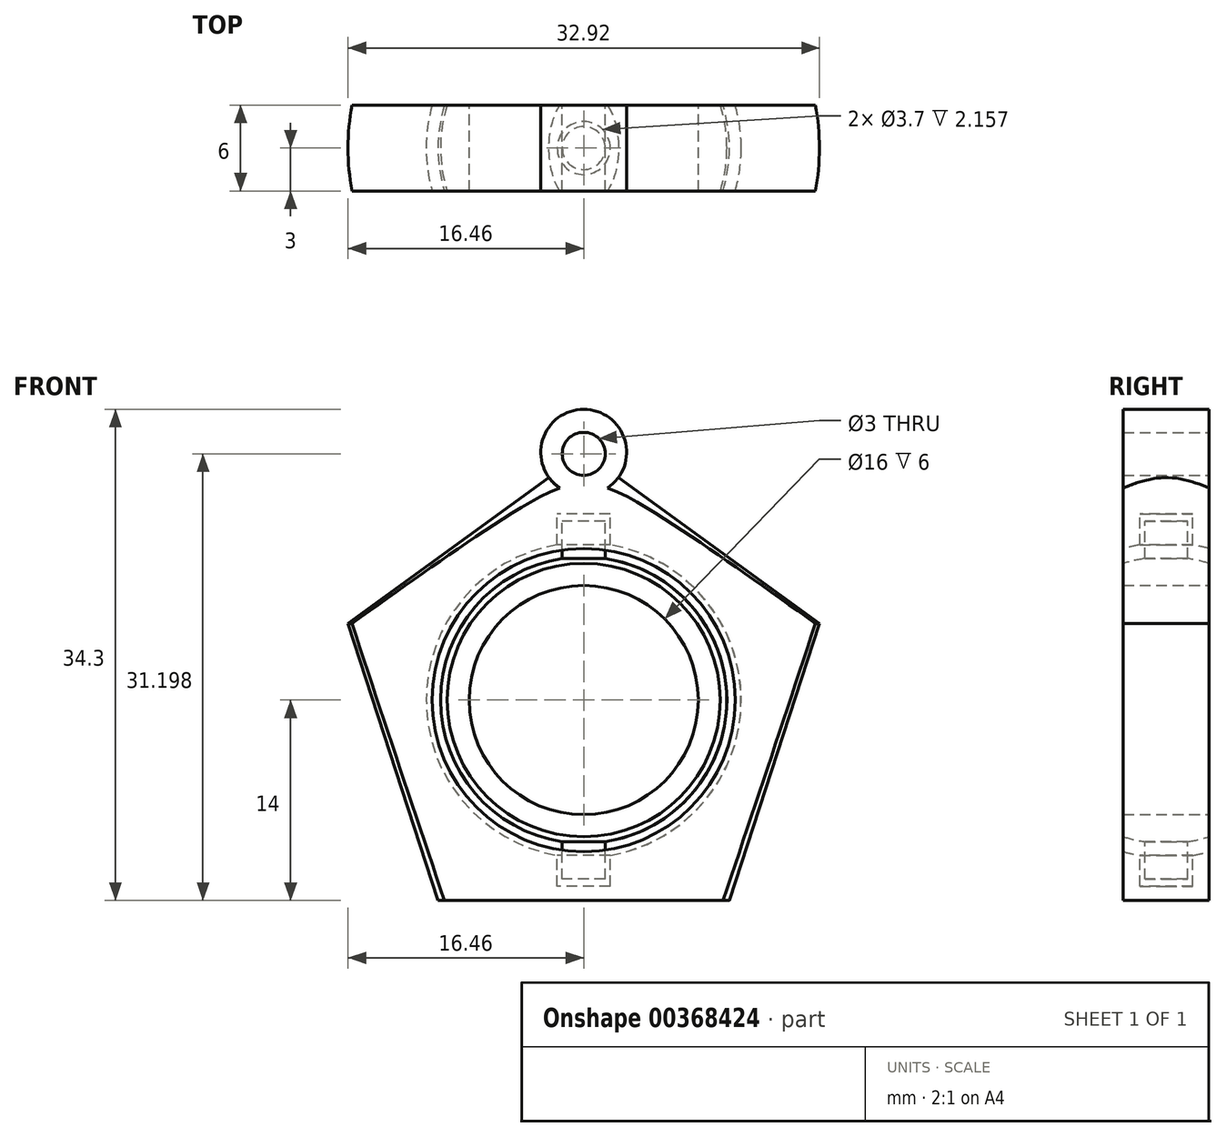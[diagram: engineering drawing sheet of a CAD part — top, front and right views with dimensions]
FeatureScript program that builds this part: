
annotation { "Feature Type Name" : "Feature", "Feature Type Description" : "" }
export const myFeature = defineFeature(function(context is Context, id is Id, definition is map)
    precondition{}
    {
        {
            var Q0;
            Q0=qCreatedBy(makeId("Front.planeOp"),FACE);
            var sketch = newSketch(context, id + "F0", { "sketchPlane" : qUnion([Q0])});
            skLineSegment(sketch, "E0.bottom", {"start": v(-1.85, 13) * mm, "end": v(1.85, 13) * mm});
            skLineSegment(sketch, "E0.top", {"start": v(-1.85, -13) * mm, "end": v(1.85, -13) * mm});
            skLineSegment(sketch, "E0.left", {"start": v(-1.85, 13) * mm, "end": v(-1.85, -13) * mm});
            skLineSegment(sketch, "E0.right", {"start": v(1.85, 13) * mm, "end": v(1.85, -13) * mm});
            skPoint(sketch, "E0.middle", {"position": v(0, 0) * mm});
            skLineSegment(sketch, "E1.bottom", {"start": v(-1.5, 12.5) * mm, "end": v(1.5, 12.5) * mm});
            skLineSegment(sketch, "E1.top", {"start": v(-1.5, -12.5) * mm, "end": v(1.5, -12.5) * mm});
            skLineSegment(sketch, "E1.left", {"start": v(-1.5, 12.5) * mm, "end": v(-1.5, -12.5) * mm});
            skLineSegment(sketch, "E1.right", {"start": v(1.5, 12.5) * mm, "end": v(1.5, -12.5) * mm});
            skCircle(sketch, "E2.cCircle", {"center": v(0, 0) * mm, "radius": 14 * mm, "construction": true});
            skLineSegment(sketch, "E2.0", {"start": v(0, 17.3) * mm, "end": v(16.46, 5.35) * mm});
            skLineSegment(sketch, "E2.1", {"start": v(16.46, 5.35) * mm, "end": v(10.17, -14) * mm});
            skLineSegment(sketch, "E2.2", {"start": v(10.17, -14) * mm, "end": v(-10.17, -14) * mm});
            skLineSegment(sketch, "E2.3", {"start": v(-10.17, -14) * mm, "end": v(-16.46, 5.35) * mm});
            skLineSegment(sketch, "E2.4", {"start": v(-16.46, 5.35) * mm, "end": v(0, 17.3) * mm});
            skPoint(sketch, "E2.0.midPoint", {"position": v(8.23, 11.33) * mm});
            skCircle(sketch, "E3", {"center": v(0, 0) * mm, "radius": 10 * mm});
            skCircle(sketch, "E4", {"center": v(0, 0) * mm, "radius": 11 * mm});
            skSolve(sketch);
        }
        {
            var Q0;
            Q0=qCreatedBy(makeId("Front.planeOp"),FACE);
            var sketch = newSketch(context, id + "F1", { "sketchPlane" : qUnion([Q0])});
            skLineSegment(sketch, "E5.0", {"start": v(-16.46, 5.35) * mm, "end": v(0, 17.3) * mm});
            skArc(sketch, "E5.1", {"start": v(-1.85, 9.83) * mm, "mid": v(-10, -0.18) * mm, "end": v(-1.5, -9.89) * mm});
            skArc(sketch, "E5.2", {"start": v(-1.85, 10.84) * mm, "mid": v(-11, 0) * mm, "end": v(-1.85, -10.84) * mm});
            skLineSegment(sketch, "E5.3", {"start": v(-1.85, 13) * mm, "end": v(1.85, 13) * mm});
            skLineSegment(sketch, "E5.4", {"start": v(-1.85, -13) * mm, "end": v(1.85, -13) * mm});
            skLineSegment(sketch, "E5.5", {"start": v(-1.85, 13) * mm, "end": v(-1.85, 10.84) * mm});
            skLineSegment(sketch, "E5.6", {"start": v(1.85, 13) * mm, "end": v(1.85, 10.84) * mm});
            skLineSegment(sketch, "E5.7", {"start": v(-1.5, 12.5) * mm, "end": v(1.5, 12.5) * mm});
            skLineSegment(sketch, "E5.8", {"start": v(-1.5, -12.5) * mm, "end": v(1.5, -12.5) * mm});
            skLineSegment(sketch, "E5.9", {"start": v(-1.5, 12.5) * mm, "end": v(-1.5, 9.89) * mm});
            skLineSegment(sketch, "E5.10", {"start": v(1.5, 12.5) * mm, "end": v(1.5, 9.89) * mm});
            skLineSegment(sketch, "E5.12", {"start": v(0, 17.3) * mm, "end": v(16.46, 5.35) * mm});
            skLineSegment(sketch, "E5.13", {"start": v(16.46, 5.35) * mm, "end": v(10.17, -14) * mm});
            skLineSegment(sketch, "E5.14", {"start": v(10.17, -14) * mm, "end": v(-10.17, -14) * mm});
            skLineSegment(sketch, "E5.15", {"start": v(-10.17, -14) * mm, "end": v(-16.46, 5.35) * mm});
            skArc(sketch, "E6.trimOffspring", {"start": v(1.5, -9.89) * mm, "mid": v(10, 0) * mm, "end": v(1.5, 9.89) * mm});
            skArc(sketch, "E7.trimOffspring", {"start": v(1.85, -10.84) * mm, "mid": v(11, 0) * mm, "end": v(1.85, 10.84) * mm});
            skLineSegment(sketch, "E8.trimOffspring", {"start": v(-1.85, -10.84) * mm, "end": v(-1.85, -13) * mm});
            skLineSegment(sketch, "E9.trimOffspring", {"start": v(1.85, -10.84) * mm, "end": v(1.85, -13) * mm});
            skLineSegment(sketch, "E10.trimOffspring", {"start": v(1.5, -9.89) * mm, "end": v(1.5, -12.5) * mm});
            skLineSegment(sketch, "E11.trimOffspring", {"start": v(-1.5, -9.89) * mm, "end": v(-1.5, -12.5) * mm});
            skArc(sketch, "E12.13", {"start": v(-1.5, 9.89) * mm, "mid": v(-10, 0) * mm, "end": v(-1.5, -9.89) * mm});
            skArc(sketch, "E13.trimOffspring", {"start": v(1.85, 9.83) * mm, "mid": v(1.68, 9.86) * mm, "end": v(1.5, 9.89) * mm});
            skArc(sketch, "E14.trimOffspring", {"start": v(1.5, -9.89) * mm, "mid": v(1.68, -9.86) * mm, "end": v(1.85, -9.83) * mm});
            skArc(sketch, "E15.trimOffspring", {"start": v(1.5, -9.89) * mm, "mid": v(10, -0.18) * mm, "end": v(1.85, 9.83) * mm});
            skSolve(sketch);
        }
        {
            var Q0;
            Q0=qCreatedBy(makeId("Front.planeOp"),FACE);
            var sketch = newSketch(context, id + "F2", { "sketchPlane" : qUnion([Q0])});
            skLineSegment(sketch, "E16.4", {"start": v(16.46, 5.35) * mm, "end": v(10.17, -14) * mm});
            skLineSegment(sketch, "E16.6", {"start": v(1.5, 12.5) * mm, "end": v(1.5, 9.89) * mm});
            skArc(sketch, "E16.11", {"start": v(1.5, -9.89) * mm, "mid": v(10, -0.18) * mm, "end": v(1.85, 9.83) * mm});
            skLineSegment(sketch, "E16.12", {"start": v(0, 13) * mm, "end": v(1.85, 13) * mm});
            skLineSegment(sketch, "E16.14", {"start": v(10.17, -14) * mm, "end": v(0, -14) * mm});
            skLineSegment(sketch, "E16.15", {"start": v(1.85, -10.84) * mm, "end": v(1.85, -13) * mm});
            skLineSegment(sketch, "E16.16", {"start": v(1.85, 13) * mm, "end": v(1.85, 10.84) * mm});
            skArc(sketch, "E16.17", {"start": v(1.85, -10.84) * mm, "mid": v(11, 0) * mm, "end": v(1.85, 10.84) * mm});
            skLineSegment(sketch, "E16.20", {"start": v(0, 17.3) * mm, "end": v(16.46, 5.35) * mm});
            skLineSegment(sketch, "E16.21", {"start": v(1.5, -9.89) * mm, "end": v(1.5, -12.5) * mm});
            skLineSegment(sketch, "E16.22", {"start": v(1.5, 12.5) * mm, "end": v(1.5, 9.89) * mm});
            skLineSegment(sketch, "E16.25", {"start": v(1.85, 13) * mm, "end": v(1.85, 10.84) * mm});
            skLineSegment(sketch, "E16.27", {"start": v(16.46, 5.35) * mm, "end": v(10.17, -14) * mm});
            skLineSegment(sketch, "E16.28", {"start": v(0, 13) * mm, "end": v(1.85, 13) * mm});
            skLineSegment(sketch, "E16.30", {"start": v(1.85, -10.84) * mm, "end": v(1.85, -13) * mm});
            skArc(sketch, "E16.31", {"start": v(1.5, -9.89) * mm, "mid": v(10, 0) * mm, "end": v(1.5, 9.89) * mm});
            skLineSegment(sketch, "E16.33", {"start": v(0, 12.5) * mm, "end": v(1.5, 12.5) * mm});
            skLineSegment(sketch, "E16.34", {"start": v(1.5, -9.89) * mm, "end": v(1.5, -12.5) * mm});
            skLineSegment(sketch, "E16.35", {"start": v(0, 17.3) * mm, "end": v(16.46, 5.35) * mm});
            skArc(sketch, "E16.39", {"start": v(1.85, -10.84) * mm, "mid": v(11, 0) * mm, "end": v(1.85, 10.84) * mm});
            skLineSegment(sketch, "E16.43", {"start": v(1.85, -10.84) * mm, "end": v(1.85, -13) * mm});
            skLineSegment(sketch, "E16.45", {"start": v(1.5, 12.5) * mm, "end": v(1.5, 9.89) * mm});
            skLineSegment(sketch, "E16.46", {"start": v(1.85, 13) * mm, "end": v(1.85, 10.84) * mm});
            skArc(sketch, "E16.47", {"start": v(1.85, -10.84) * mm, "mid": v(11, 0) * mm, "end": v(1.85, 10.84) * mm});
            skLineSegment(sketch, "E16.49", {"start": v(16.46, 5.35) * mm, "end": v(10.17, -14) * mm});
            skArc(sketch, "E16.54", {"start": v(1.85, -10.84) * mm, "mid": v(11, 0) * mm, "end": v(1.85, 10.84) * mm});
            skPoint(sketch, "E16.51.end.orphan", {"position": v(-16.46, 5.35) * mm});
            skPoint(sketch, "E16.51.start.orphan", {"position": v(-10.17, -14) * mm});
            skPoint(sketch, "E16.23.end.orphan", {"position": v(0, 17.3) * mm});
            skPoint(sketch, "E16.23.start.orphan", {"position": v(-16.46, 5.35) * mm});
            skPoint(sketch, "E16.13.end.orphan", {"position": v(0, 17.3) * mm});
            skPoint(sketch, "E16.13.start.orphan", {"position": v(-16.46, 5.35) * mm});
            skPoint(sketch, "E16.10.end.orphan", {"position": v(-16.46, 5.35) * mm});
            skPoint(sketch, "E16.10.start.orphan", {"position": v(-10.17, -14) * mm});
            skPoint(sketch, "E16.42.end.orphan", {"position": v(-16.46, 5.35) * mm});
            skPoint(sketch, "E16.42.start.orphan", {"position": v(-10.17, -14) * mm});
            skPoint(sketch, "E16.2.end.orphan", {"position": v(-1.85, -10.84) * mm});
            skPoint(sketch, "E16.2.start.orphan", {"position": v(-1.85, 10.84) * mm});
            skPoint(sketch, "E16.24.end.orphan", {"position": v(-1.85, -10.84) * mm});
            skPoint(sketch, "E16.24.start.orphan", {"position": v(-1.85, 10.84) * mm});
            skPoint(sketch, "E16.41.end.orphan", {"position": v(-1.5, -9.89) * mm});
            skPoint(sketch, "E16.3.end.orphan", {"position": v(-1.5, -9.89) * mm});
            skPoint(sketch, "E16.3.start.orphan", {"position": v(-1.85, 9.83) * mm});
            skPoint(sketch, "E16.38.end.orphan", {"position": v(-1.5, -12.5) * mm});
            skPoint(sketch, "E16.38.start.orphan", {"position": v(-1.5, -9.89) * mm});
            skPoint(sketch, "E16.48.end.orphan", {"position": v(-1.5, -12.5) * mm});
            skPoint(sketch, "E16.48.start.orphan", {"position": v(-1.5, -9.89) * mm});
            skPoint(sketch, "E16.5.end.orphan", {"position": v(-1.5, -12.5) * mm});
            skPoint(sketch, "E16.5.start.orphan", {"position": v(-1.5, -9.89) * mm});
            skPoint(sketch, "E16.50.end.orphan", {"position": v(-1.85, -13) * mm});
            skPoint(sketch, "E16.50.start.orphan", {"position": v(-1.85, -10.84) * mm});
            skPoint(sketch, "E16.26.end.orphan", {"position": v(-1.85, -13) * mm});
            skPoint(sketch, "E16.26.start.orphan", {"position": v(-1.85, -10.84) * mm});
            skPoint(sketch, "E16.8.end.orphan", {"position": v(-1.85, -13) * mm});
            skPoint(sketch, "E16.8.start.orphan", {"position": v(-1.85, -10.84) * mm});
            skPoint(sketch, "E16.32.end.orphan", {"position": v(-1.5, 9.89) * mm});
            skPoint(sketch, "E16.32.start.orphan", {"position": v(-1.5, 12.5) * mm});
            skPoint(sketch, "E16.29.end.orphan", {"position": v(-1.85, 10.84) * mm});
            skPoint(sketch, "E16.29.start.orphan", {"position": v(-1.85, 13) * mm});
            skPoint(sketch, "E16.9.end.orphan", {"position": v(-1.5, 9.89) * mm});
            skPoint(sketch, "E16.9.start.orphan", {"position": v(-1.5, 12.5) * mm});
            skPoint(sketch, "E16.53.end.orphan", {"position": v(-1.85, 10.84) * mm});
            skPoint(sketch, "E16.53.start.orphan", {"position": v(-1.85, 13) * mm});
            skPoint(sketch, "E16.18.end.orphan", {"position": v(-1.85, 10.84) * mm});
            skPoint(sketch, "E16.18.start.orphan", {"position": v(-1.85, 13) * mm});
            skPoint(sketch, "E16.19.end.orphan", {"position": v(-1.85, 9.83) * mm});
            skPoint(sketch, "E16.19.start.orphan", {"position": v(-1.5, 9.89) * mm});
            skLineSegment(sketch, "E17", {"start": v(0, -12.5) * mm, "end": v(1.5, -12.5) * mm});
            skLineSegment(sketch, "E18", {"start": v(0, -13) * mm, "end": v(1.85, -13) * mm});
            skPoint(sketch, "E16.52.end.orphan", {"position": v(1.85, -13) * mm});
            skPoint(sketch, "E16.1.start.orphan", {"position": v(-1.85, -13) * mm});
            skPoint(sketch, "E16.40.end.orphan", {"position": v(1.85, -13) * mm});
            skPoint(sketch, "E16.7.end.orphan", {"position": v(1.5, -12.5) * mm});
            skPoint(sketch, "E16.36.start.orphan", {"position": v(-1.5, -12.5) * mm});
            skPoint(sketch, "E16.37.start.orphan", {"position": v(10.17, -14) * mm});
            skPoint(sketch, "E16.44.start.orphan", {"position": v(-1.85, 13) * mm});
            skPoint(sketch, "E16.0.start.orphan", {"position": v(-1.5, 12.5) * mm});
            skLineSegment(sketch, "E19", {"start": v(0, 17.3) * mm, "end": v(0, 13) * mm});
            skLineSegment(sketch, "E20", {"start": v(0, 12.5) * mm, "end": v(0, -12.5) * mm});
            skLineSegment(sketch, "E21", {"start": v(0, -13) * mm, "end": v(0, -14) * mm});
            skSolve(sketch);
        }
        {
            var Q0;
            Q0 = qSketchRegion(id + "F2", true);
            var Q1;
            Q1=sQuery(id+"F2.wireOp",EDGE,"E20");
            revolve(context, id + "F3", {"entities" : qUnion([Q0]), "axis" : qUnion([Q1]), "revolveType" : RevolveType.FULL});
        }
        {
            var Q0;
            Q0=qCreatedBy(makeId("Right.planeOp"),FACE);
            var sketch = newSketch(context, id + "F4", { "sketchPlane" : qUnion([Q0])});
            skLineSegment(sketch, "E22.bottom", {"start": v(-3, 18.47) * mm, "end": v(-21.65, 18.47) * mm});
            skLineSegment(sketch, "E22.top", {"start": v(-3, -16.6) * mm, "end": v(-21.65, -16.6) * mm});
            skLineSegment(sketch, "E22.left", {"start": v(-3, 18.47) * mm, "end": v(-3, -16.6) * mm});
            skLineSegment(sketch, "E22.right", {"start": v(-21.65, 18.47) * mm, "end": v(-21.65, -16.6) * mm});
            skLineSegment(sketch, "E23.bottom", {"start": v(3, 18.1) * mm, "end": v(19.4, 18.1) * mm});
            skLineSegment(sketch, "E23.top", {"start": v(3, -16.98) * mm, "end": v(19.4, -16.98) * mm});
            skLineSegment(sketch, "E23.left", {"start": v(3, 18.1) * mm, "end": v(3, -16.98) * mm});
            skLineSegment(sketch, "E23.right", {"start": v(19.4, 18.1) * mm, "end": v(19.4, -16.98) * mm});
            skSolve(sketch);
        }
        {
            var Q0;
            Q0 = qSketchRegion(id + "F4", true);
            extrude(context, id + "F5", {"entities" : qUnion([Q0]), "operationType" : NewBodyOperationType.REMOVE, "endBound" : BoundingType.SYMMETRIC, "oppositeDirection" : true, "depth" : 50 * mm});
        }
        {
            var Q0;
            Q0=qCreatedBy(makeId("Front.planeOp"),FACE);
            var sketch = newSketch(context, id + "F6", { "sketchPlane" : qUnion([Q0])});
            skCircle(sketch, "E24", {"center": v(0, 17.3) * mm, "radius": 3 * mm});
            skSolve(sketch);
        }
        {
            var Q0;
            Q0 = qSketchRegion(id + "F6", true);
            extrude(context, id + "F7", {"entities" : qUnion([Q0]), "operationType" : NewBodyOperationType.ADD, "endBound" : BoundingType.SYMMETRIC, "depth" : 6 * mm});
        }
        {
            var Q0;
            Q0=qCreatedBy(makeId("Front.planeOp"),FACE);
            var sketch = newSketch(context, id + "F8", { "sketchPlane" : qUnion([Q0])});
            skCircle(sketch, "E25", {"center": v(0, 0) * mm, "radius": 8 * mm});
            skCircle(sketch, "E26", {"center": v(0, 17.2) * mm, "radius": 1.5 * mm});
            skSolve(sketch);
        }
        {
            var Q0;
            Q0 = qSketchRegion(id + "F8", true);
            extrude(context, id + "F9", {"entities" : qUnion([Q0]), "operationType" : NewBodyOperationType.REMOVE, "endBound" : BoundingType.SYMMETRIC, "depth" : 25 * mm});
        }
    });
